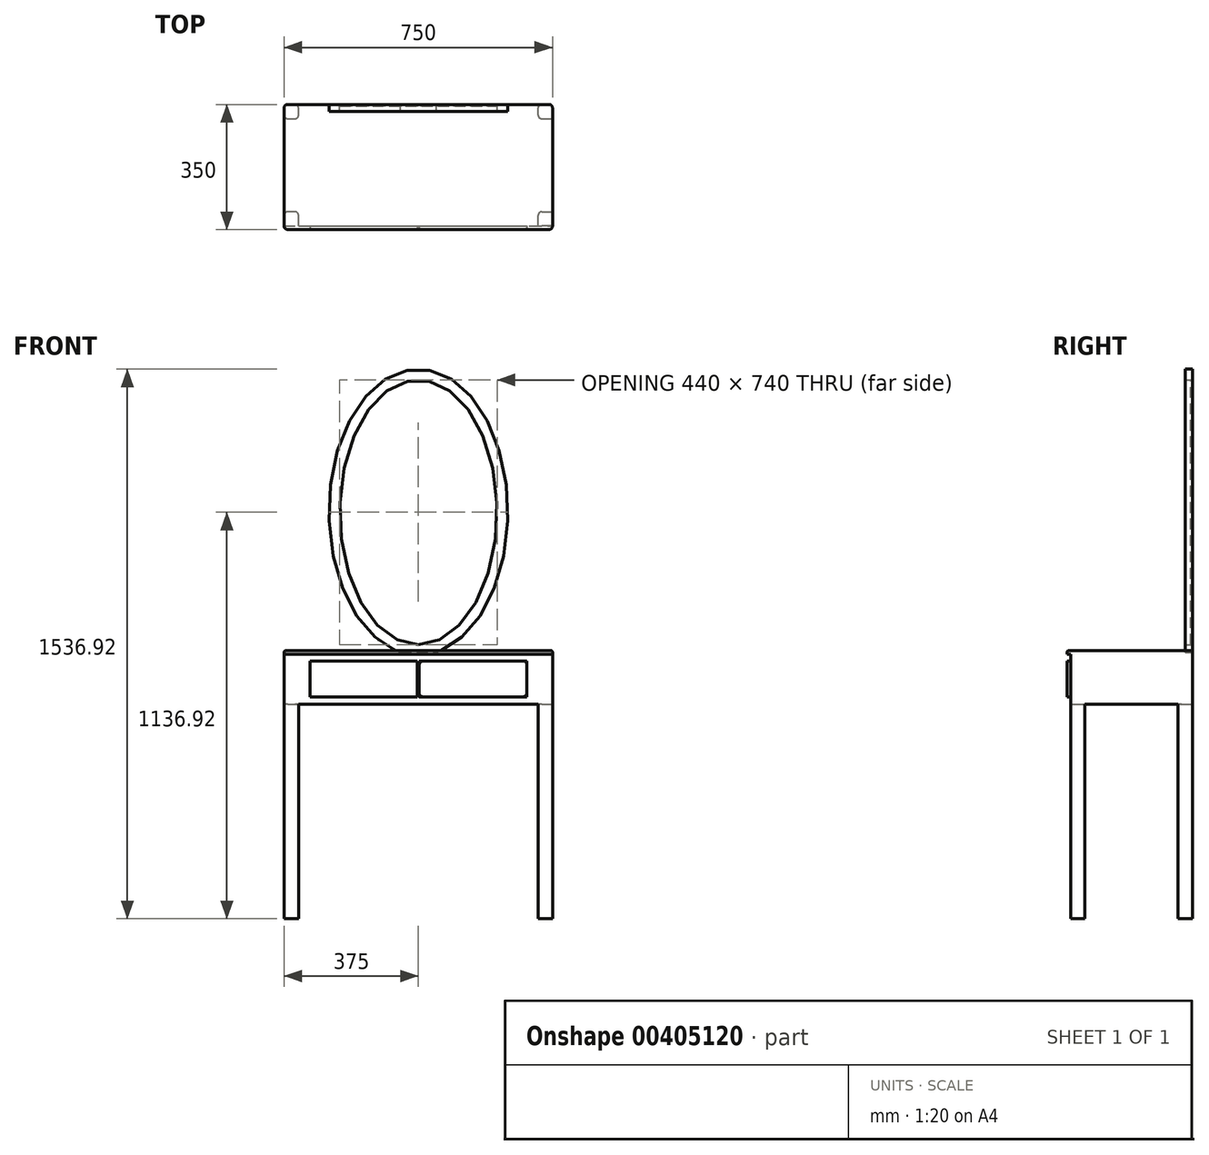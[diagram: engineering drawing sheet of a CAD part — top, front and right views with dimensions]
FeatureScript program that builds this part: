
annotation { "Feature Type Name" : "Feature", "Feature Type Description" : "" }
export const myFeature = defineFeature(function(context is Context, id is Id, definition is map)
    precondition{}
    {
        {
            var Q0;
            Q0=qCreatedBy(makeId("Front.planeOp"),FACE);
            var sketch = newSketch(context, id + "F0", { "sketchPlane" : qUnion([Q0])});
            skLineSegment(sketch, "E0.bottom", {"start": v(-375, 750) * mm, "end": v(375, 750) * mm});
            skLineSegment(sketch, "E0.top", {"start": v(-335, 600) * mm, "end": v(335, 600) * mm});
            skLineSegment(sketch, "E0.left", {"start": v(-375, 750) * mm, "end": v(-375, 600) * mm});
            skLineSegment(sketch, "E0.right", {"start": v(375, 750) * mm, "end": v(375, 600) * mm});
            skLineSegment(sketch, "E1.top", {"start": v(-375, 0) * mm, "end": v(-335, 0) * mm});
            skLineSegment(sketch, "E1.left", {"start": v(-375, 600) * mm, "end": v(-375, 0) * mm});
            skLineSegment(sketch, "E1.right", {"start": v(-335, 600) * mm, "end": v(-335, 0) * mm});
            skLineSegment(sketch, "E2.top", {"start": v(375, 0) * mm, "end": v(335, 0) * mm});
            skLineSegment(sketch, "E2.left", {"start": v(375, 600) * mm, "end": v(375, 0) * mm});
            skLineSegment(sketch, "E2.right", {"start": v(335, 600) * mm, "end": v(335, 0) * mm});
            skLineSegment(sketch, "E3", {"start": v(0, 0) * mm, "end": v(0, 150.8) * mm, "construction": true});
            skSolve(sketch);
        }
        {
            var Q0;
            Q0=qSketchRegion(id+"F0",true);
            extrude(context, id + "F1", {"entities" : qUnion([Q0]), "depth" : 350 * mm});
        }
        {
            var Q0;
            Q0=makeQuery(id+"F1.opExtrude","SWEPT_FACE",FACE,{"disambiguationData":[OSD([sQuery(id+"F0.wireOp",EDGE,"E0.right"),sQuery(id+"F0.wireOp",EDGE,"E2.left")])]});
            var sketch = newSketch(context, id + "F2", { "sketchPlane" : qUnion([Q0])});
            skLineSegment(sketch, "E4.bottom", {"start": v(-300, -10) * mm, "end": v(-40, -10) * mm});
            skLineSegment(sketch, "E4.top", {"start": v(-300, 600) * mm, "end": v(-40, 600) * mm});
            skLineSegment(sketch, "E4.left", {"start": v(-300, -10) * mm, "end": v(-300, 600) * mm});
            skLineSegment(sketch, "E4.right", {"start": v(-40, -10) * mm, "end": v(-40, 600) * mm});
            skSolve(sketch);
        }
        {
            var Q0;
            Q0=qSketchRegion(id+"F2",true);
            extrude(context, id + "F3", {"entities" : qUnion([Q0]), "operationType" : NewBodyOperationType.REMOVE, "endBound" : BoundingType.THROUGH_ALL, "oppositeDirection" : true, "depth" : 25 * mm});
        }
        {
            var Q0;
            Q0=makeQuery(id+"F1.opExtrude","CAP_FACE",FACE,{"disambiguationData":[OSD([sQuery(id+"F0.wireOp",EDGE,"E0.bottom"),sQuery(id+"F0.wireOp",EDGE,"E0.top"),sQuery(id+"F0.wireOp",EDGE,"E0.left"),sQuery(id+"F0.wireOp",EDGE,"E0.right"),sQuery(id+"F0.wireOp",EDGE,"E1.top"),sQuery(id+"F0.wireOp",EDGE,"E1.left"),sQuery(id+"F0.wireOp",EDGE,"E1.right"),sQuery(id+"F0.wireOp",EDGE,"E2.top"),sQuery(id+"F0.wireOp",EDGE,"E2.left"),sQuery(id+"F0.wireOp",EDGE,"E2.right")])],"isStart":false});
            var sketch = newSketch(context, id + "F4", { "sketchPlane" : qUnion([Q0])});
            skLineSegment(sketch, "E5.bottom", {"start": v(-302.5, 720) * mm, "end": v(-2.5, 720) * mm});
            skLineSegment(sketch, "E5.top", {"start": v(-302.5, 620) * mm, "end": v(-2.5, 620) * mm});
            skLineSegment(sketch, "E5.left", {"start": v(-302.5, 720) * mm, "end": v(-302.5, 620) * mm});
            skLineSegment(sketch, "E5.right", {"start": v(-2.5, 720) * mm, "end": v(-2.5, 620) * mm});
            skLineSegment(sketch, "E6.bottom", {"start": v(2.5, 720) * mm, "end": v(302.5, 720) * mm});
            skLineSegment(sketch, "E6.top", {"start": v(2.5, 620) * mm, "end": v(302.5, 620) * mm});
            skLineSegment(sketch, "E6.left", {"start": v(2.5, 720) * mm, "end": v(2.5, 620) * mm});
            skLineSegment(sketch, "E6.right", {"start": v(302.5, 720) * mm, "end": v(302.5, 620) * mm});
            skLineSegment(sketch, "E7.bottom", {"start": v(-385, 760) * mm, "end": v(385, 760) * mm});
            skLineSegment(sketch, "E7.top", {"start": v(-385, 740) * mm, "end": v(385, 740) * mm});
            skLineSegment(sketch, "E7.left", {"start": v(-385, 760) * mm, "end": v(-385, 740) * mm});
            skLineSegment(sketch, "E7.right", {"start": v(385, 760) * mm, "end": v(385, 740) * mm});
            skSolve(sketch);
        }
        {
            var Q0;
            Q0=makeQuery(id+"F4.imprint","IMPRINT",FACE,{"disambiguationData":[TD([[makeQuery(id+"F4.imprint","IMPRINT",EDGE,{"derivedFrom":sQuery(id+"F4.wireOp",EDGE,"E5.bottom")}),1.0]])]});
            extrude(context, id + "F5", {"entities" : qUnion([Q0]), "operationType" : NewBodyOperationType.REMOVE, "oppositeDirection" : true, "depth" : 10 * mm});
        }
        {
            var Q0;
            Q0=makeQuery(id+"F1.opExtrude","CAP_EDGE",EDGE,{"disambiguationData":[OSD([sQuery(id+"F0.wireOp",EDGE,"E0.left"),sQuery(id+"F0.wireOp",EDGE,"E1.left")])],"isStart":true});
            var Q1;
            Q1=makeQuery(id+"F5.boolean.opBoolean","COPY",EDGE,{"derivedFrom":makeQuery(id+"F5.opExtrude","CAP_EDGE",EDGE,{"disambiguationData":[OSD([sQuery(id+"F0.wireOp",EDGE,"E0.left"),sQuery(id+"F0.wireOp",EDGE,"E1.left")])],"isStart":false})});
            var Q2;
            Q2=makeQuery(id+"F5.boolean.opBoolean","COPY",EDGE,{"derivedFrom":makeQuery(id+"F5.opExtrude","CAP_EDGE",EDGE,{"disambiguationData":[OSD([sQuery(id+"F0.wireOp",EDGE,"E0.right"),sQuery(id+"F0.wireOp",EDGE,"E2.left")])],"isStart":false})});
            var Q3;
            Q3=makeQuery(id+"F1.opExtrude","CAP_EDGE",EDGE,{"disambiguationData":[OSD([sQuery(id+"F0.wireOp",EDGE,"E0.right"),sQuery(id+"F0.wireOp",EDGE,"E2.left")])],"isStart":true});
            var Q4;
            Q4=makeQuery(id+"F3.boolean.opBoolean","INTERSECT",EDGE,{"derivedFrom":[makeQuery(id+"F1.opExtrude","SWEPT_FACE",FACE,{"disambiguationData":[OSD([sQuery(id+"F0.wireOp",EDGE,"E2.right")])]}),makeQuery(id+"F3.opExtrude","SWEPT_FACE",FACE,{"disambiguationData":[OSD([sQuery(id+"F2.wireOp",EDGE,"E4.right")])]})]});
            var Q5;
            Q5=makeQuery(id+"F1.opExtrude","CAP_EDGE",EDGE,{"disambiguationData":[OSD([sQuery(id+"F0.wireOp",EDGE,"E2.right")])],"isStart":true});
            var Q6;
            Q6=makeQuery(id+"F3.boolean.opBoolean","COPY",EDGE,{"derivedFrom":makeQuery(id+"F3.opExtrude","CAP_EDGE",EDGE,{"disambiguationData":[OSD([sQuery(id+"F2.wireOp",EDGE,"E4.right")])],"isStart":true})});
            var Q7;
            Q7=makeQuery(id+"F1.opExtrude","CAP_EDGE",EDGE,{"disambiguationData":[OSD([sQuery(id+"F0.wireOp",EDGE,"E1.right")])],"isStart":true});
            var Q8;
            Q8=makeQuery(id+"F3.boolean.opBoolean","INTERSECT",EDGE,{"derivedFrom":[makeQuery(id+"F1.opExtrude","SWEPT_FACE",FACE,{"disambiguationData":[OSD([sQuery(id+"F0.wireOp",EDGE,"E1.right")])]}),makeQuery(id+"F3.opExtrude","SWEPT_FACE",FACE,{"disambiguationData":[OSD([sQuery(id+"F2.wireOp",EDGE,"E4.right")])]})]});
            var Q9;
            Q9=makeQuery(id+"F3.boolean.opBoolean","INTERSECT",EDGE,{"derivedFrom":[makeQuery(id+"F1.opExtrude","SWEPT_FACE",FACE,{"disambiguationData":[OSD([sQuery(id+"F0.wireOp",EDGE,"E0.left"),sQuery(id+"F0.wireOp",EDGE,"E1.left")])]}),makeQuery(id+"F3.opExtrude","SWEPT_FACE",FACE,{"disambiguationData":[OSD([sQuery(id+"F2.wireOp",EDGE,"E4.right")])]})]});
            var Q10;
            Q10=makeQuery(id+"F3.boolean.opBoolean","COPY",EDGE,{"derivedFrom":makeQuery(id+"F3.opExtrude","CAP_EDGE",EDGE,{"disambiguationData":[OSD([sQuery(id+"F2.wireOp",EDGE,"E4.left")])],"isStart":true})});
            var Q11;
            Q11=makeQuery(id+"F3.boolean.opBoolean","INTERSECT",EDGE,{"derivedFrom":[makeQuery(id+"F1.opExtrude","SWEPT_FACE",FACE,{"disambiguationData":[OSD([sQuery(id+"F0.wireOp",EDGE,"E2.right")])]}),makeQuery(id+"F3.opExtrude","SWEPT_FACE",FACE,{"disambiguationData":[OSD([sQuery(id+"F2.wireOp",EDGE,"E4.left")])]})]});
            var Q12;
            Q12=makeQuery(id+"F5.boolean.opBoolean","COPY",EDGE,{"derivedFrom":makeQuery(id+"F5.opExtrude","CAP_EDGE",EDGE,{"disambiguationData":[OSD([sQuery(id+"F0.wireOp",EDGE,"E2.right")])],"isStart":false})});
            var Q13;
            Q13=makeQuery(id+"F5.boolean.opBoolean","COPY",EDGE,{"derivedFrom":makeQuery(id+"F5.opExtrude","CAP_EDGE",EDGE,{"disambiguationData":[OSD([sQuery(id+"F0.wireOp",EDGE,"E1.right")])],"isStart":false})});
            var Q14;
            Q14=makeQuery(id+"F3.boolean.opBoolean","INTERSECT",EDGE,{"derivedFrom":[makeQuery(id+"F1.opExtrude","SWEPT_FACE",FACE,{"disambiguationData":[OSD([sQuery(id+"F0.wireOp",EDGE,"E1.right")])]}),makeQuery(id+"F3.opExtrude","SWEPT_FACE",FACE,{"disambiguationData":[OSD([sQuery(id+"F2.wireOp",EDGE,"E4.left")])]})]});
            var Q15;
            Q15=makeQuery(id+"F3.boolean.opBoolean","INTERSECT",EDGE,{"derivedFrom":[makeQuery(id+"F1.opExtrude","SWEPT_FACE",FACE,{"disambiguationData":[OSD([sQuery(id+"F0.wireOp",EDGE,"E0.left"),sQuery(id+"F0.wireOp",EDGE,"E1.left")])]}),makeQuery(id+"F3.opExtrude","SWEPT_FACE",FACE,{"disambiguationData":[OSD([sQuery(id+"F2.wireOp",EDGE,"E4.left")])]})]});
            var Q16;
            Q16=makeQuery(id+"F1.opExtrude","CAP_EDGE",EDGE,{"disambiguationData":[OSD([sQuery(id+"F0.wireOp",EDGE,"E0.right"),sQuery(id+"F0.wireOp",EDGE,"E2.left")])],"isStart":false});
            var Q17;
            Q17=makeQuery(id+"F1.opExtrude","CAP_EDGE",EDGE,{"disambiguationData":[OSD([sQuery(id+"F0.wireOp",EDGE,"E0.left"),sQuery(id+"F0.wireOp",EDGE,"E1.left")])],"isStart":false});
            fillet(context, id + "F6", {"entities" : qUnion([Q0, Q1, Q2, Q3, Q4, Q5, Q6, Q7, Q8, Q9, Q10, Q11, Q12, Q13, Q14, Q15, Q16, Q17]), "radius" : 10 * mm, "tangentPropagation" : true, "allowEdgeOverflow" : false});
        }
        {
            var Q0;
            Q0=makeQuery(id+"F5.boolean.opBoolean","COPY",EDGE,{"derivedFrom":makeQuery(id+"F5.opExtrude","CAP_EDGE",EDGE,{"disambiguationData":[OSD([sQuery(id+"F4.wireOp",EDGE,"E6.top")])],"isStart":true})});
            var Q1;
            Q1=makeQuery(id+"F5.boolean.opBoolean","COPY",EDGE,{"derivedFrom":makeQuery(id+"F5.opExtrude","CAP_EDGE",EDGE,{"disambiguationData":[OSD([sQuery(id+"F4.wireOp",EDGE,"E6.right")])],"isStart":true})});
            var Q2;
            Q2=makeQuery(id+"F5.boolean.opBoolean","COPY",EDGE,{"derivedFrom":makeQuery(id+"F5.opExtrude","CAP_EDGE",EDGE,{"disambiguationData":[OSD([sQuery(id+"F4.wireOp",EDGE,"E6.bottom")])],"isStart":true})});
            var Q3;
            Q3=makeQuery(id+"F5.boolean.opBoolean","COPY",EDGE,{"derivedFrom":makeQuery(id+"F5.opExtrude","CAP_EDGE",EDGE,{"disambiguationData":[OSD([sQuery(id+"F4.wireOp",EDGE,"E6.left")])],"isStart":true})});
            var Q4;
            Q4=makeQuery(id+"F5.boolean.opBoolean","COPY",EDGE,{"derivedFrom":makeQuery(id+"F5.opExtrude","CAP_EDGE",EDGE,{"disambiguationData":[OSD([sQuery(id+"F4.wireOp",EDGE,"E5.right")])],"isStart":true})});
            var Q5;
            Q5=makeQuery(id+"F5.boolean.opBoolean","COPY",EDGE,{"derivedFrom":makeQuery(id+"F5.opExtrude","CAP_EDGE",EDGE,{"disambiguationData":[OSD([sQuery(id+"F4.wireOp",EDGE,"E5.top")])],"isStart":true})});
            var Q6;
            Q6=makeQuery(id+"F5.boolean.opBoolean","COPY",EDGE,{"derivedFrom":makeQuery(id+"F5.opExtrude","CAP_EDGE",EDGE,{"disambiguationData":[OSD([sQuery(id+"F4.wireOp",EDGE,"E5.left")])],"isStart":true})});
            var Q7;
            Q7=makeQuery(id+"F5.boolean.opBoolean","COPY",EDGE,{"derivedFrom":makeQuery(id+"F5.opExtrude","CAP_EDGE",EDGE,{"disambiguationData":[OSD([sQuery(id+"F4.wireOp",EDGE,"E5.bottom")])],"isStart":true})});
            fillet(context, id + "F7", {"entities" : qUnion([Q0, Q1, Q2, Q3, Q4, Q5, Q6, Q7]), "radius" : 5 * mm, "tangentPropagation" : true, "allowEdgeOverflow" : false});
        }
        {
            var Q0;
            Q0=makeQuery(id+"F1.opExtrude","CAP_EDGE",EDGE,{"disambiguationData":[OSD([sQuery(id+"F0.wireOp",EDGE,"E0.bottom")])],"isStart":false});
            fillet(context, id + "F8", {"entities" : qUnion([Q0]), "radius" : 5 * mm, "tangentPropagation" : true, "allowEdgeOverflow" : false});
        }
        {
            var Q0;
            Q0=makeQuery(id+"F1.opExtrude","CAP_FACE",FACE,{"disambiguationData":[OSD([sQuery(id+"F0.wireOp",EDGE,"E0.bottom"),sQuery(id+"F0.wireOp",EDGE,"E0.top"),sQuery(id+"F0.wireOp",EDGE,"E0.left"),sQuery(id+"F0.wireOp",EDGE,"E0.right"),sQuery(id+"F0.wireOp",EDGE,"E1.top"),sQuery(id+"F0.wireOp",EDGE,"E1.left"),sQuery(id+"F0.wireOp",EDGE,"E1.right"),sQuery(id+"F0.wireOp",EDGE,"E2.top"),sQuery(id+"F0.wireOp",EDGE,"E2.left"),sQuery(id+"F0.wireOp",EDGE,"E2.right")])],"isStart":true});
            var sketch = newSketch(context, id + "F9", { "sketchPlane" : qUnion([Q0])});
            skEllipse(sketch, "E8", {"center": v(0, 1136.92) * mm, "majorRadius": 400 * mm, "minorRadius": 250 * mm, "majorAxis": v(0, -1)});
            skLineSegment(sketch, "E9", {"start": v(-50, 745) * mm, "end": v(50, 745) * mm, "construction": true});
            skLineSegment(sketch, "E10", {"start": v(0, 1136.92) * mm, "end": v(0, 736.92) * mm, "construction": true});
            skLineSegment(sketch, "E11", {"start": v(0, 1136.92) * mm, "end": v(250, 1136.92) * mm, "construction": true});
            skEllipse(sketch, "E12", {"center": v(0, 1136.92) * mm, "majorRadius": 370 * mm, "minorRadius": 220 * mm, "majorAxis": v(0, -1)});
            skLineSegment(sketch, "E13", {"start": v(0, 1136.92) * mm, "end": v(220, 1136.92) * mm, "construction": true});
            skLineSegment(sketch, "E14", {"start": v(0, 1136.92) * mm, "end": v(0, 766.92) * mm, "construction": true});
            skSolve(sketch);
        }
        {
            var Q0;
            Q0=makeQuery(id+"F9.imprint","IMPRINT",FACE,{"disambiguationData":[TD([[makeQuery(id+"F9.imprint","IMPRINT",EDGE,{"derivedFrom":sQuery(id+"F9.wireOp",EDGE,"E12")}),1.0]])]});
            extrude(context, id + "F10", {"entities" : qUnion([Q0]), "oppositeDirection" : true, "depth" : 5 * mm});
        }
        {
            var Q0;
            Q0=makeQuery(id+"F9.imprint","IMPRINT",FACE,{"disambiguationData":[TD([[makeQuery(id+"F9.imprint","IMPRINT",EDGE,{"derivedFrom":sQuery(id+"F9.wireOp",EDGE,"E12")}),-1.0]])]});
            extrude(context, id + "F11", {"entities" : qUnion([Q0]), "oppositeDirection" : true, "depth" : 20 * mm});
        }
    });
